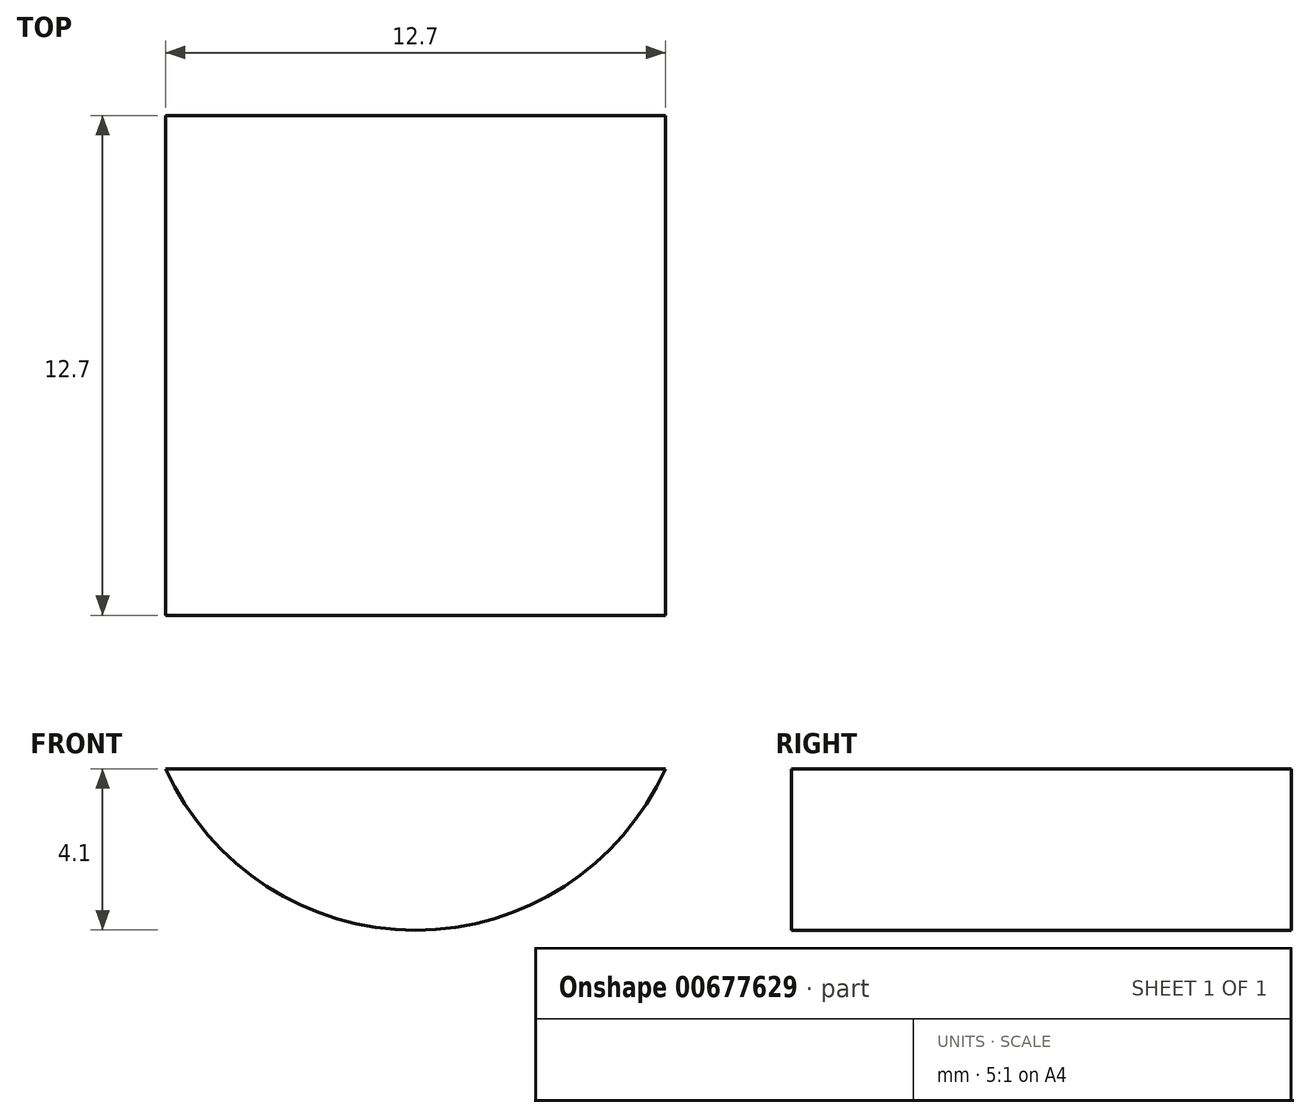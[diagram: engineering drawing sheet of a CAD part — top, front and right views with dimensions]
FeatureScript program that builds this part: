
annotation { "Feature Type Name" : "Feature", "Feature Type Description" : "" }
export const myFeature = defineFeature(function(context is Context, id is Id, definition is map)
    precondition{}
    {
        {
            var Q0;
            Q0=qCreatedBy(makeId("Front.planeOp"),FACE);
            var sketch = newSketch(context, id + "F0", { "sketchPlane" : qUnion([Q0])});
            skLineSegment(sketch, "E0", {"start": v(-6.35, 0) * mm, "end": v(6.35, 0) * mm});
            skArc(sketch, "E1", {"start": v(-6.35, 0) * mm, "mid": v(0, -4.1) * mm, "end": v(6.35, 0) * mm});
            skSolve(sketch);
        }
        {
            var Q0;
            Q0 = qSketchRegion(id + "F0", true);
            extrude(context, id + "F1", {"entities" : qUnion([Q0]), "depth" : 12.7 * mm, "offsetDistance" : 25.4 * mm});
        }
    });
